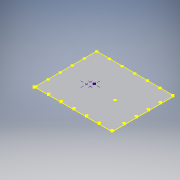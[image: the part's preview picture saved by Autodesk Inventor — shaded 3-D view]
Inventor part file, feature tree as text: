
AUTODESK INVENTOR PART (.ipt)
format: ipt  version: 2017 (Build 210142000, 142)  size: 201,728 bytes
history: native  units: in
note: dims shown in document units (in); Inventor stores cm internally (conversion verified against a paired STEP export)
features: sketch x5, hole x4, pattern_linear x4, extrude x1
ambient origin geometry x8: Origin, YZ Plane, XZ Plane, XY Plane, X Axis, Y Axis, Z Axis, Center Point
bodies: Solid1 (feature_tree)
feature tree (14):
  extrude  "Extrusion1"  Depth=8.0in
  sketch  "Sketch2"  dims[d4=0.06in d5=0.0in]
  hole  "Hole1"  [1 undecoded]
  pattern_linear  "Rectangular Pattern1"  Count1=7 Spacing1=1.635in
  pattern_linear  "Rectangular Pattern2"  Count1=5 Spacing1=1.562in
  hole  "Hole2"  [1 undecoded]
  pattern_linear  "Rectangular Pattern3"  Count1=5 Spacing1=1.562in
  pattern_linear  "Rectangular Pattern4"  Count1=7 Spacing1=1.635in
  sketch  "Sketch3"  dims[d6=0.096in d7=0.75in d8=0.16in d9=0.25in d10=0.5635in d11=1.0in d12=0.8108in d13=0.0935in]
  sketch  "Sketch6"  dims[d14=0.0935in d15=2.7559in d17=1.635in d18=1.9685in d20=1.562in]
  sketch  "Sketch7"  dims[d21=0.0935in d22=0.0935in d23=0.096in d24=0.75in d25=0.16in d26=0.25in d27=0.5635in d28=1.0in d29=0.8108in d30=1.9685in d32=1.562in d33=2.7559in d35=1.635in d36=0.128in d37=0.75in d38=0.232in d39=0.25in d40=0.5635in d41=0.06in d42=0.8108in d43=0.128in d44=0.75in d45=0.232in d46=0.25in d47=0.5635in d48=1.0in d49=0.8108in d50=3.656in d51=4.156in d52=3.062in d53=3.562in]
  hole  "Hole3"  [1 undecoded]
  hole  "Hole4"  [1 undecoded]
  sketch  "Sketch1"  dims[d0=10.0in d3=8.0in]
note: 4 required parameter values undecoded (feature->parameter linkage not recoverable at this tier; creation-order binding heuristic only, values carry confidence <= 0.55)
